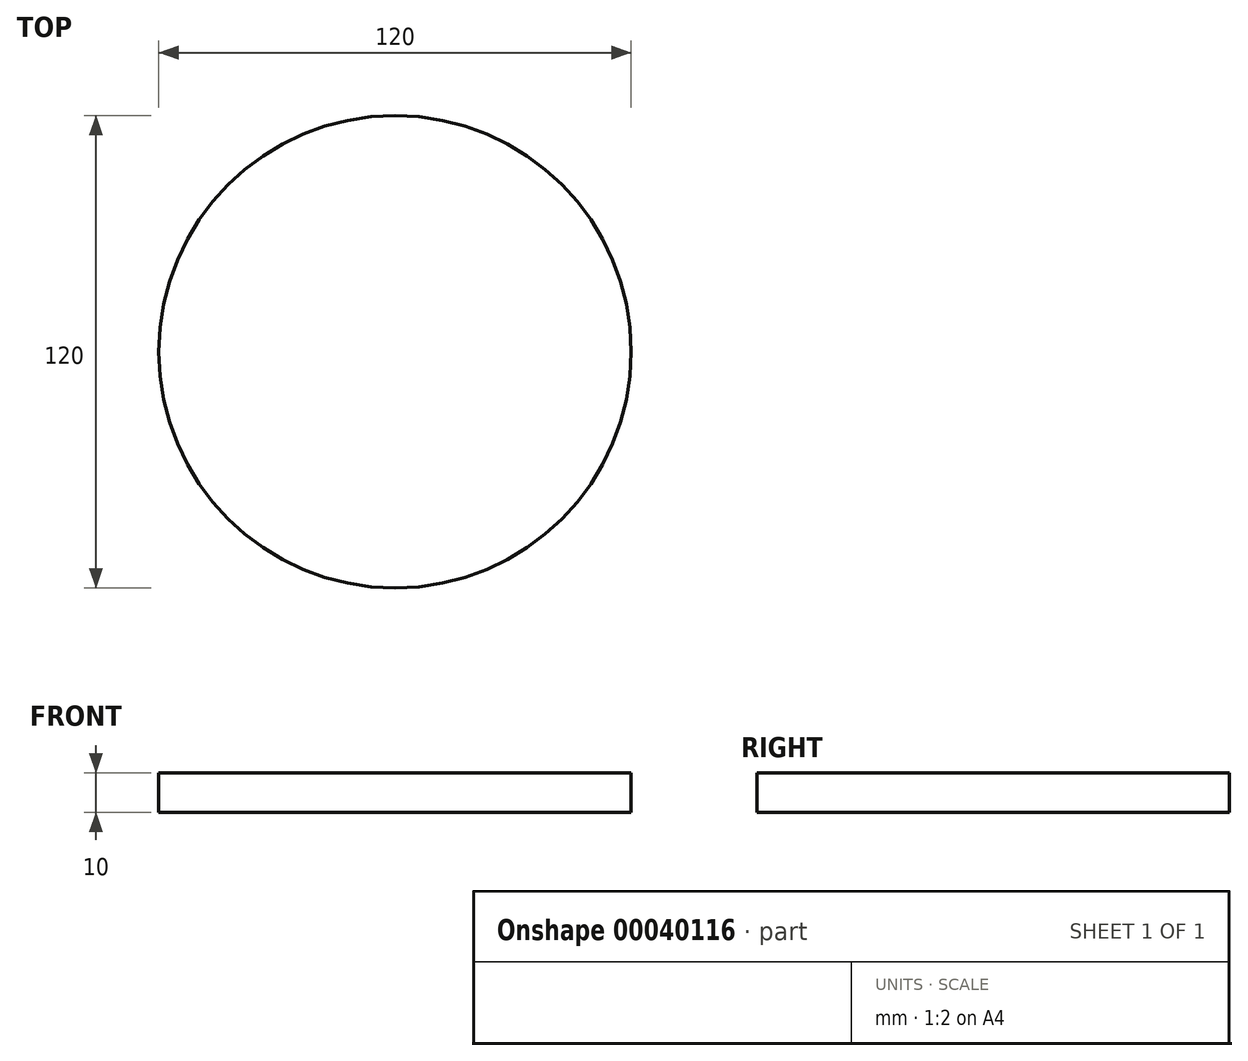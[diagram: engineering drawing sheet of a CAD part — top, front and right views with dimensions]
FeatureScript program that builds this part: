
annotation { "Feature Type Name" : "Feature", "Feature Type Description" : "" }
export const myFeature = defineFeature(function(context is Context, id is Id, definition is map)
    precondition{}
    {
        {
            var Q0;
            Q0=qCreatedBy(makeId("Top.planeOp"),FACE);
            var sketch = newSketch(context, id + "F0", { "sketchPlane" : qUnion([Q0])});
            skCircle(sketch, "E0", {"center": v(0, 0) * mm, "radius": 60 * mm});
            skSolve(sketch);
        }
        {
            var Q0;
            Q0=sQuery(id+"F0.wireOp",EDGE,"E0");
            extrude(context, id + "F1", {"bodyType" : ToolBodyType.SURFACE, "surfaceEntities" : qUnion([Q0]), "depth" : 10 * mm});
        }
    });
